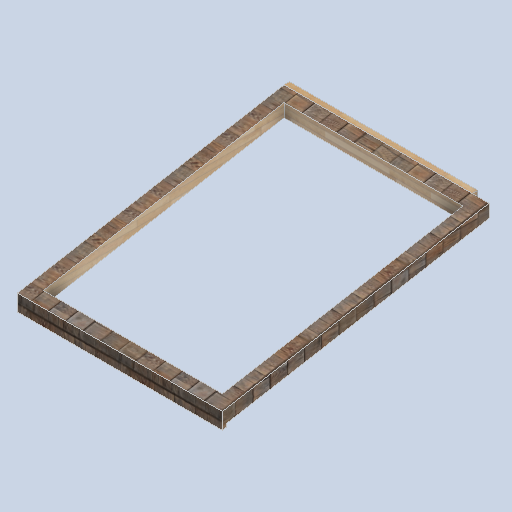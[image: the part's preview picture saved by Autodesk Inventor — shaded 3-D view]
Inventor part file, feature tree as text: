
AUTODESK INVENTOR PART (.ipt)
format: ipt  version: 2024.2 (Build 282272000, 272)  size: 202,240 bytes
history: native  units: in
note: dims shown in document units (in); Inventor stores cm internally (conversion verified against a paired STEP export)
features: sketch x7, plane x5, other x3
ambient origin geometry x8: Origin, YZ Plane, XZ Plane, XY Plane, X Axis, Y Axis, Z Axis, Center Point
bodies: Solid1 (feature_tree)
feature tree (15):
  other  "eave_frame_02_MIR.ipt"
  other  "Solid1::eave_frame_02_MIR.ipt"
  other  "TaggingFeature1"
  sketch  "Sketch3"  dims[d0=0.3937in]
  sketch  "Sketch4"
  sketch  "Sketch5"
  sketch  "Sketch6"
  sketch  "Sketch7"
  sketch  "Sketch8"
  sketch  "Sketch9"
  plane  "Work Plane1"
  plane  "Work Plane2"
  plane  "Work Plane3"
  plane  "Work Plane4"
  plane  "Work Plane5"
